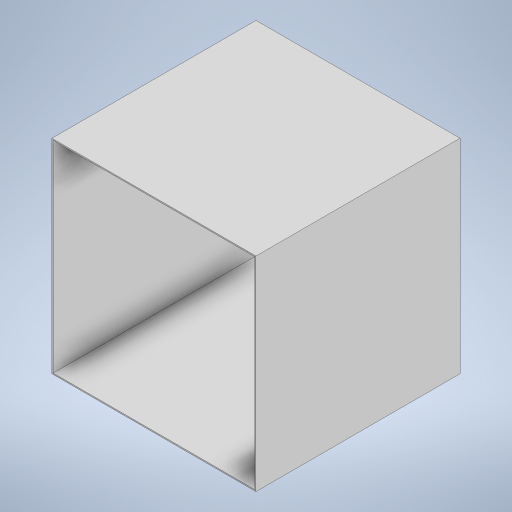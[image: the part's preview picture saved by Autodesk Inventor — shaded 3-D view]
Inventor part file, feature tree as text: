
AUTODESK INVENTOR PART (.ipt)
format: ipt  version: 2024 (Build 280153000, 153)  size: 184,832 bytes
history: native  units: mm
features: extrude x2, other x1, sketch x1
ambient origin geometry x8: Origin, YZ Plane, XZ Plane, XY Plane, X Axis, Y Axis, Z Axis, Center Point
bodies: Body1 (feature_tree)
feature tree (4):
  other  "Sólido1"
  sketch  "Boceto1"  dims[d0=400.0mm d1=400.0mm d2=395.0mm d3=395.0mm d4=5.0mm d5=0.0mm d6=400.0mm d7=0.0mm]
  extrude  "Extrusión1"  Depth=400.0mm
  extrude  "Extrusión2"  Depth=395.0mm
